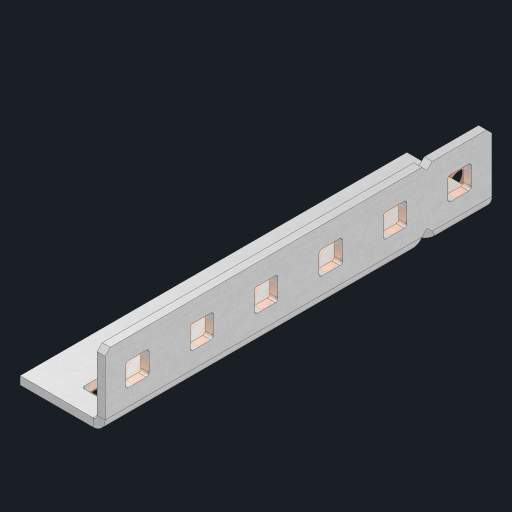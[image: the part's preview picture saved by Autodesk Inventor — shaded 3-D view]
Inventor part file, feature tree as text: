
AUTODESK INVENTOR PART (.ipt)
format: ipt  version: 2023 (Build 270158000, 158)  size: 520,704 bytes
history: native  units: in
note: dims shown in document units (in); Inventor stores cm internally (conversion verified against a paired STEP export)
features: other x17, extrude x11, sheet_metal_op x10, sketch x8, mirror x1, pattern_linear x1, chamfer x1
ambient origin geometry x8: Origin, YZ Plane, XZ Plane, XY Plane, X Axis, Y Axis, Z Axis, Center Point
bodies: Solid1 (feature_tree), Body (feature_tree)
feature tree (49):
  other  "Flange Pattern Plane"
  sheet_metal_op  "Flange Pattern"
  sheet_metal_op  "Body Pattern"
  other  "Arc Length"
  mirror  "Notch Mirror"
  pattern_linear  "Notch Pattern"  Spacing1=0.25in  [1 undecoded]
  chamfer  "End Chamfer"
  extrude  "Half Cut"  Depth=0.0625in
  sketch  "Sketch1"  dims[d0=1.5in]
  other  "Plate1"
  sketch  "Sketch2"  dims[d1=3.0in]
  other  "Plate2"
  sheet_metal_op  "Bend1"
  sheet_metal_op  "Corner1"
  sketch  "Sketch3"  dims[d2=0.0625in]
  other  "Flange Pattern Sketch"
  sketch  "Sketch7"  dims[d3=0.0625in]
  other  "Srf1"
  other  "Srf2"
  sketch  "Sketch8"  dims[d4=0.0312in]
  sketch  "Sketch9"  dims[d5=0.125in]
  other  "Srf91"
  sheet_metal_op  "Body Pattern Sketch"
  other  "Srf92"
  sketch  "Sketch13"  dims[d6=0.0625in]
  sketch  "Sketch14"  dims[d7=0.5in d8=90.0deg d9=0.0312in d10=0.25in d11=0.0625in d12=0.0625in d16=0.182in d17=0.02in d18=0.0625in d19=0.0in d20=0.25in d21=0.25in d46=0.172in d47=1.0in d48=0.0in d49=0.182in d50=0.02in d51=0.25in d52=0.25in d53=0.0625in d54=0.0in d55=0.172in d56=1.0in d57=0.0in d60=2.3622in d62=0.5in d63=0.3937in d65=0.5in d85=0.1473in d86=0.1782in d88=0.04in d89=0.0625in d90=0.0in d91=0.04in d92=0.0491in d95=2.5in d96=0.04in d97=0.25in d98=45.0deg d101=0.0in d102=2.497in d131=0.5in d132=2.3622in d134=0.5in d139=0.5in]
  other  "Srf856"
  other  "Srf1310"
  other  "Srf1311"
  other  "Srf1312"
  other  "Srf1376"
  other  "Srf1377"
  other  "Srf1728"
  other  "Srf1755"
  sheet_metal_op  "Flange Stamp"
  sheet_metal_op  "Flange Circle"
  sheet_metal_op  "Body Stamp"
  sheet_metal_op  "Body Circle"
  sheet_metal_op  "Notch"
  extrude  "ExtrusionSrf2"  Depth=0.0625in
  extrude  "ExtrusionSrf92"  Depth=0.5in
  extrude  "ExtrusionSrf856"  Depth=0.02in
  extrude  "ExtrusionSrf1310"  Depth=0.0625in
  extrude  "ExtrusionSrf1311"  TaperAngle=0.0deg  [1 undecoded]
  extrude  "ExtrusionSrf1312"  Depth=0.5in
  extrude  "ExtrusionSrf1376"  Depth=0.5in
  extrude  "ExtrusionSrf1377"  Depth=0.5in
  extrude  "ExtrusionSrf1728"  Depth=0.5in TaperAngle=0.0deg
  extrude  "ExtrusionSrf1755"  Depth=0.5in
note: 2 required parameter values undecoded (feature->parameter linkage not recoverable at this tier; creation-order binding heuristic only, values carry confidence <= 0.55)
